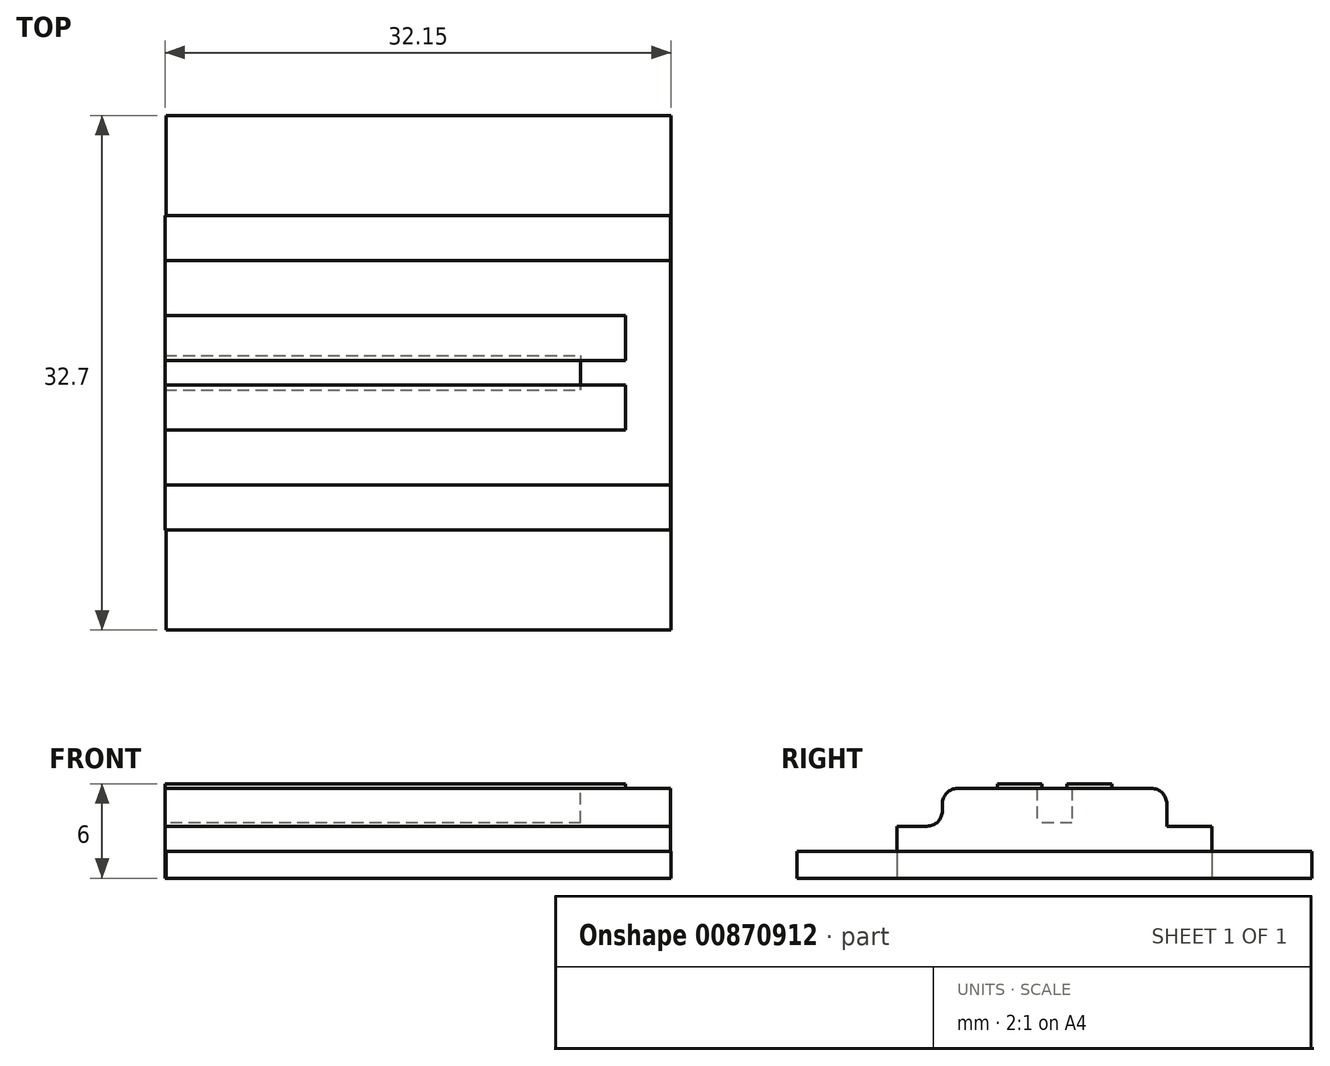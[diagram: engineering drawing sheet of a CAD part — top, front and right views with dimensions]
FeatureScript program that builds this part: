
annotation { "Feature Type Name" : "Feature", "Feature Type Description" : "" }
export const myFeature = defineFeature(function(context is Context, id is Id, definition is map)
    precondition{}
    {
        {
            var Q0;
            Q0=qCreatedBy(makeId("Top.planeOp"),FACE);
            var sketch = newSketch(context, id + "F0", { "sketchPlane" : qUnion([Q0])});
            skLineSegment(sketch, "E0.bottom", {"start": v(28.55, -10) * mm, "end": v(-28.55, -10) * mm});
            skLineSegment(sketch, "E0.top", {"start": v(28.55, 10) * mm, "end": v(-28.55, 10) * mm});
            skLineSegment(sketch, "E0.left", {"start": v(28.55, -10) * mm, "end": v(28.55, 10) * mm});
            skLineSegment(sketch, "E0.right", {"start": v(-28.55, -10) * mm, "end": v(-28.55, 10) * mm});
            skPoint(sketch, "E0.middle", {"position": v(0, 0) * mm});
            skSolve(sketch);
        }
        {
            var Q0;
            Q0=makeQuery(id+"F0.imprint","IMPRINT",FACE,{"disambiguationData":[TD([[makeQuery(id+"F0.imprint","IMPRINT",EDGE,{"derivedFrom":sQuery(id+"F0.wireOp",EDGE,"E0.bottom")}),-1.0]])]});
            extrude(context, id + "F1", {"entities" : qUnion([Q0]), "depth" : 3.3 * mm, "offsetDistance" : 25 * mm});
        }
        {
            var Q0;
            Q0=makeQuery(id+"F1.opExtrude","CAP_FACE",FACE,{"disambiguationData":[OSD([sQuery(id+"F0.wireOp",EDGE,"E0.bottom"),sQuery(id+"F0.wireOp",EDGE,"E0.top"),sQuery(id+"F0.wireOp",EDGE,"E0.left"),sQuery(id+"F0.wireOp",EDGE,"E0.right")])],"isStart":false});
            var sketch = newSketch(context, id + "F2", { "sketchPlane" : qUnion([Q0])});
            skLineSegment(sketch, "E1.bottom", {"start": v(28.55, -7.13) * mm, "end": v(-28.55, -7.13) * mm});
            skLineSegment(sketch, "E1.top", {"start": v(28.55, 7.13) * mm, "end": v(-28.55, 7.13) * mm});
            skLineSegment(sketch, "E1.left", {"start": v(28.55, -7.13) * mm, "end": v(28.55, 7.13) * mm});
            skLineSegment(sketch, "E1.right", {"start": v(-28.55, -7.13) * mm, "end": v(-28.55, 7.13) * mm});
            skPoint(sketch, "E1.middle", {"position": v(0, 0) * mm});
            skSolve(sketch);
        }
        {
            var Q0;
            Q0=makeQuery(id+"F2.imprint","IMPRINT",FACE,{"disambiguationData":[TD([[makeQuery(id+"F2.imprint","IMPRINT",EDGE,{"derivedFrom":sQuery(id+"F2.wireOp",EDGE,"E1.bottom")}),-1.0]])]});
            extrude(context, id + "F3", {"entities" : qUnion([Q0]), "operationType" : NewBodyOperationType.ADD, "depth" : 2.4 * mm, "offsetDistance" : 25 * mm});
        }
        {
            var Q0;
            Q0=makeQuery(id+"F3.opExtrude","CAP_EDGE",EDGE,{"disambiguationData":[OSD([sQuery(id+"F2.wireOp",EDGE,"E1.bottom")])],"isStart":true});
            var Q1;
            Q1=makeQuery(id+"F3.opExtrude","CAP_EDGE",EDGE,{"disambiguationData":[OSD([sQuery(id+"F2.wireOp",EDGE,"E1.top")])],"isStart":true});
            var Q2;
            Q2=makeQuery(id+"F3.opExtrude","CAP_EDGE",EDGE,{"disambiguationData":[OSD([sQuery(id+"F2.wireOp",EDGE,"E1.top")])],"isStart":false});
            var Q3;
            Q3=makeQuery(id+"F3.opExtrude","CAP_EDGE",EDGE,{"disambiguationData":[OSD([sQuery(id+"F2.wireOp",EDGE,"E1.bottom")])],"isStart":false});
            fillet(context, id + "F4", {"entities" : qUnion([Q0, Q1, Q2, Q3]), "radius" : 0.98 * mm, "tangentPropagation" : true, "allowEdgeOverflow" : false});
        }
        {
            var Q0;
            Q0=makeQuery(id+"F3.boolean.opBoolean","MERGE",FACE,{"derivedFrom":[makeQuery(id+"F1.opExtrude","SWEPT_FACE",FACE,{"disambiguationData":[OSD([sQuery(id+"F0.wireOp",EDGE,"E0.right")])]}),makeQuery(id+"F3.opExtrude","SWEPT_FACE",FACE,{"disambiguationData":[OSD([sQuery(id+"F2.wireOp",EDGE,"E1.right")])]})]});
            var sketch = newSketch(context, id + "F5", { "sketchPlane" : qUnion([Q0])});
            skLineSegment(sketch, "E2.bottom", {"start": v(1.11, 3.52) * mm, "end": v(-1.11, 3.52) * mm});
            skLineSegment(sketch, "E2.top", {"start": v(1.11, 7.88) * mm, "end": v(-1.11, 7.88) * mm});
            skLineSegment(sketch, "E2.left", {"start": v(1.11, 3.52) * mm, "end": v(1.11, 7.88) * mm});
            skLineSegment(sketch, "E2.right", {"start": v(-1.11, 3.52) * mm, "end": v(-1.11, 7.88) * mm});
            skPoint(sketch, "E2.middle", {"position": v(0, 5.7) * mm});
            skSolve(sketch);
        }
        {
            var Q0;
            Q0=qSketchRegion(id+"F5",true);
            extrude(context, id + "F6", {"entities" : qUnion([Q0]), "operationType" : NewBodyOperationType.REMOVE, "oppositeDirection" : true, "depth" : 51.4 * mm, "offsetDistance" : 25 * mm});
        }
        {
            var Q0;
            Q0=makeQuery(id+"F3.opExtrude","CAP_FACE",FACE,{"disambiguationData":[OSD([sQuery(id+"F2.wireOp",EDGE,"E1.bottom"),sQuery(id+"F2.wireOp",EDGE,"E1.top"),sQuery(id+"F2.wireOp",EDGE,"E1.left"),sQuery(id+"F2.wireOp",EDGE,"E1.right")])],"isStart":false});
            var sketch = newSketch(context, id + "F7", { "sketchPlane" : qUnion([Q0])});
            skLineSegment(sketch, "E3.bottom", {"start": v(-28.55, 3.63) * mm, "end": v(25.7, 3.63) * mm});
            skLineSegment(sketch, "E3.top", {"start": v(-28.55, 0.8) * mm, "end": v(25.7, 0.8) * mm});
            skLineSegment(sketch, "E3.left", {"start": v(-28.55, 3.63) * mm, "end": v(-28.55, 0.8) * mm});
            skLineSegment(sketch, "E3.right", {"start": v(25.7, 3.63) * mm, "end": v(25.7, 0.8) * mm});
            skLineSegment(sketch, "E4.MirrorCS", {"start": v(-28.55, -0.8) * mm, "end": v(25.7, -0.8) * mm});
            skLineSegment(sketch, "E5.MirrorCS", {"start": v(25.7, -3.63) * mm, "end": v(25.7, -0.8) * mm});
            skLineSegment(sketch, "E6.MirrorCS", {"start": v(-28.55, -3.63) * mm, "end": v(25.7, -3.63) * mm});
            skLineSegment(sketch, "E7.MirrorCS", {"start": v(-28.55, -3.63) * mm, "end": v(-28.55, -0.8) * mm});
            skSolve(sketch);
        }
        {
            var Q0;
            {var subQ8=sQuery(id+"F7.wireOp",EDGE,"E3.bottom");Q0=makeQuery(id+"F7.imprint","IMPRINT",FACE,{"disambiguationData":[TD([[makeQuery(id+"F7.imprint","IMPRINT",EDGE,{"derivedFrom":subQ8}),-1.0]])]});}
            var Q1;
            {var subQ3=sQuery(id+"F5.wireOp",EDGE,"E2.right");var subQ4=makeQuery(id+"F3.opExtrude","CAP_FACE",FACE,{"disambiguationData":[OSD([sQuery(id+"F2.wireOp",EDGE,"E1.bottom"),sQuery(id+"F2.wireOp",EDGE,"E1.top"),sQuery(id+"F2.wireOp",EDGE,"E1.left"),sQuery(id+"F2.wireOp",EDGE,"E1.right")])],"isStart":false});var subQ7=makeQuery(id+"F6.boolean.opBoolean","INTERSECT",EDGE,{"derivedFrom":[subQ4,makeQuery(id+"F6.opExtrude","SWEPT_FACE",FACE,{"disambiguationData":[OSD([subQ3])]})]});Q1=makeQuery(id+"F7.imprint","IMPRINT",FACE,{"disambiguationData":[TD([[makeQuery(id+"F7.imprint","IMPRINT",EDGE,{"derivedFrom":subQ7}),-1.0]])]});}
            var Q2;
            {var subQ3=sQuery(id+"F5.wireOp",EDGE,"E2.left");var subQ4=makeQuery(id+"F3.opExtrude","CAP_FACE",FACE,{"disambiguationData":[OSD([sQuery(id+"F2.wireOp",EDGE,"E1.bottom"),sQuery(id+"F2.wireOp",EDGE,"E1.top"),sQuery(id+"F2.wireOp",EDGE,"E1.left"),sQuery(id+"F2.wireOp",EDGE,"E1.right")])],"isStart":false});var subQ7=makeQuery(id+"F6.boolean.opBoolean","INTERSECT",EDGE,{"derivedFrom":[subQ4,makeQuery(id+"F6.opExtrude","SWEPT_FACE",FACE,{"disambiguationData":[OSD([subQ3])]})]});Q2=makeQuery(id+"F7.imprint","IMPRINT",FACE,{"disambiguationData":[TD([[makeQuery(id+"F7.imprint","IMPRINT",EDGE,{"derivedFrom":subQ7}),1.0]])]});}
            var Q3;
            {var subQ9=sQuery(id+"F7.wireOp",EDGE,"E5.MirrorCS");Q3=makeQuery(id+"F7.imprint","IMPRINT",FACE,{"disambiguationData":[TD([[makeQuery(id+"F7.imprint","IMPRINT",EDGE,{"derivedFrom":subQ9}),1.0]])]});}
            extrude(context, id + "F8", {"entities" : qUnion([Q0, Q1, Q2, Q3]), "operationType" : NewBodyOperationType.ADD, "depth" : 0.3 * mm, "offsetDistance" : 25 * mm});
        }
        {
            var Q0;
            Q0=makeQuery(id+"F8.opExtrude","CAP_FACE",FACE,{"disambiguationData":[OSD([sQuery(id+"F7.wireOp",EDGE,"E4.MirrorCS"),sQuery(id+"F7.wireOp",EDGE,"E5.MirrorCS"),sQuery(id+"F7.wireOp",EDGE,"E6.MirrorCS"),sQuery(id+"F7.wireOp",EDGE,"E7.MirrorCS")])],"isStart":false});
            var sketch = newSketch(context, id + "F9", { "sketchPlane" : qUnion([Q0])});
            skLineSegment(sketch, "E8.bottom", {"start": v(-18.23, -0.8) * mm, "end": v(-16.63, -0.8) * mm});
            skLineSegment(sketch, "E8.top", {"start": v(-18.23, -2.8) * mm, "end": v(-16.63, -2.8) * mm});
            skLineSegment(sketch, "E8.left", {"start": v(-18.23, -0.8) * mm, "end": v(-18.23, -2.8) * mm});
            skLineSegment(sketch, "E8.right", {"start": v(-16.63, -0.8) * mm, "end": v(-16.63, -2.8) * mm});
            skSolve(sketch);
        }
        {
            var Q0;
            Q0=qSketchRegion(id+"F9",true);
            extrude(context, id + "F10", {"entities" : qUnion([Q0]), "operationType" : NewBodyOperationType.REMOVE, "oppositeDirection" : true, "depth" : 1.25 * mm, "offsetDistance" : 25 * mm});
        }
        {
            var Q0;
            Q0=makeQuery(id+"F8.opExtrude","CAP_FACE",FACE,{"disambiguationData":[OSD([sQuery(id+"F7.wireOp",EDGE,"E4.MirrorCS"),sQuery(id+"F7.wireOp",EDGE,"E5.MirrorCS"),sQuery(id+"F7.wireOp",EDGE,"E6.MirrorCS"),sQuery(id+"F7.wireOp",EDGE,"E7.MirrorCS")])],"isStart":false});
            var sketch = newSketch(context, id + "F11", { "sketchPlane" : qUnion([Q0])});
            skArc(sketch, "E9", {"start": v(-18.23, -2.8) * mm, "mid": v(-17.43, -3.4) * mm, "end": v(-16.63, -2.8) * mm});
            skSolve(sketch);
        }
        {
            var Q0;
            Q0=qSketchRegion(id+"F11",true);
            var Q1;
            Q1=makeQuery(id+"F11.imprint","IMPRINT",FACE,{"disambiguationData":[TD([[makeQuery(id+"F11.imprint","IMPRINT",EDGE,{"derivedFrom":sQuery(id+"F11.wireOp",EDGE,"E9")}),1.0]])]});
            extrude(context, id + "F12", {"entities" : qUnion([Q0, Q1]), "operationType" : NewBodyOperationType.REMOVE, "oppositeDirection" : true, "depth" : 1.25 * mm, "offsetDistance" : 25 * mm});
        }
        {
            var Q0;
            Q0=makeQuery(id+"F8.boolean.opBoolean","MERGE",FACE,{"derivedFrom":[makeQuery(id+"F3.boolean.opBoolean","MERGE",FACE,{"derivedFrom":[makeQuery(id+"F1.opExtrude","SWEPT_FACE",FACE,{"disambiguationData":[OSD([sQuery(id+"F0.wireOp",EDGE,"E0.right")])]}),makeQuery(id+"F3.opExtrude","SWEPT_FACE",FACE,{"disambiguationData":[OSD([sQuery(id+"F2.wireOp",EDGE,"E1.right")])]})]}),makeQuery(id+"F8.opExtrude","SWEPT_FACE",FACE,{"disambiguationData":[OSD([sQuery(id+"F7.wireOp",EDGE,"E3.left")])]}),makeQuery(id+"F8.opExtrude","SWEPT_FACE",FACE,{"disambiguationData":[OSD([sQuery(id+"F7.wireOp",EDGE,"E7.MirrorCS")])]})]});
            var sketch = newSketch(context, id + "F13", { "sketchPlane" : qUnion([Q0])});
            skLineSegment(sketch, "E10.bottom", {"start": v(10.4, -0.98) * mm, "end": v(-10.4, -0.98) * mm});
            skLineSegment(sketch, "E10.top", {"start": v(10.4, 6.31) * mm, "end": v(-10.4, 6.31) * mm});
            skLineSegment(sketch, "E10.left", {"start": v(10.4, -0.98) * mm, "end": v(10.4, 6.31) * mm});
            skLineSegment(sketch, "E10.right", {"start": v(-10.4, -0.98) * mm, "end": v(-10.4, 6.31) * mm});
            skPoint(sketch, "E10.middle", {"position": v(0, 2.66) * mm});
            skSolve(sketch);
        }
        {
            var Q0;
            Q0 = qSketchRegion(id + "F13", true);
            extrude(context, id + "F14", {"entities" : qUnion([Q0]), "operationType" : NewBodyOperationType.REMOVE, "oppositeDirection" : true, "depth" : 25 * mm, "offsetDistance" : 25 * mm});
        }
        {
            var Q0;
            Q0=qCreatedBy(makeId("Top.planeOp"),FACE);
            var sketch = newSketch(context, id + "F15", { "sketchPlane" : qUnion([Q0])});
            skLineSegment(sketch, "E11.bottom", {"start": v(28.6, -16.35) * mm, "end": v(-3.48, -16.35) * mm});
            skLineSegment(sketch, "E11.top", {"start": v(28.6, 16.35) * mm, "end": v(-3.48, 16.35) * mm});
            skLineSegment(sketch, "E11.left", {"start": v(28.6, -16.35) * mm, "end": v(28.6, 16.35) * mm});
            skLineSegment(sketch, "E11.right", {"start": v(-3.48, -16.35) * mm, "end": v(-3.48, 16.35) * mm});
            skPoint(sketch, "E11.middle", {"position": v(12.56, 0) * mm});
            skSolve(sketch);
        }
        {
            var Q0;
            Q0=makeQuery(id+"F15.imprint","IMPRINT",FACE,{"disambiguationData":[TD([[makeQuery(id+"F15.imprint","IMPRINT",EDGE,{"derivedFrom":sQuery(id+"F15.wireOp",EDGE,"E11.bottom")}),-1.0]])]});
            extrude(context, id + "F16", {"entities" : qUnion([Q0]), "operationType" : NewBodyOperationType.ADD, "depth" : 1.7 * mm, "offsetDistance" : 25 * mm});
        }
    });
